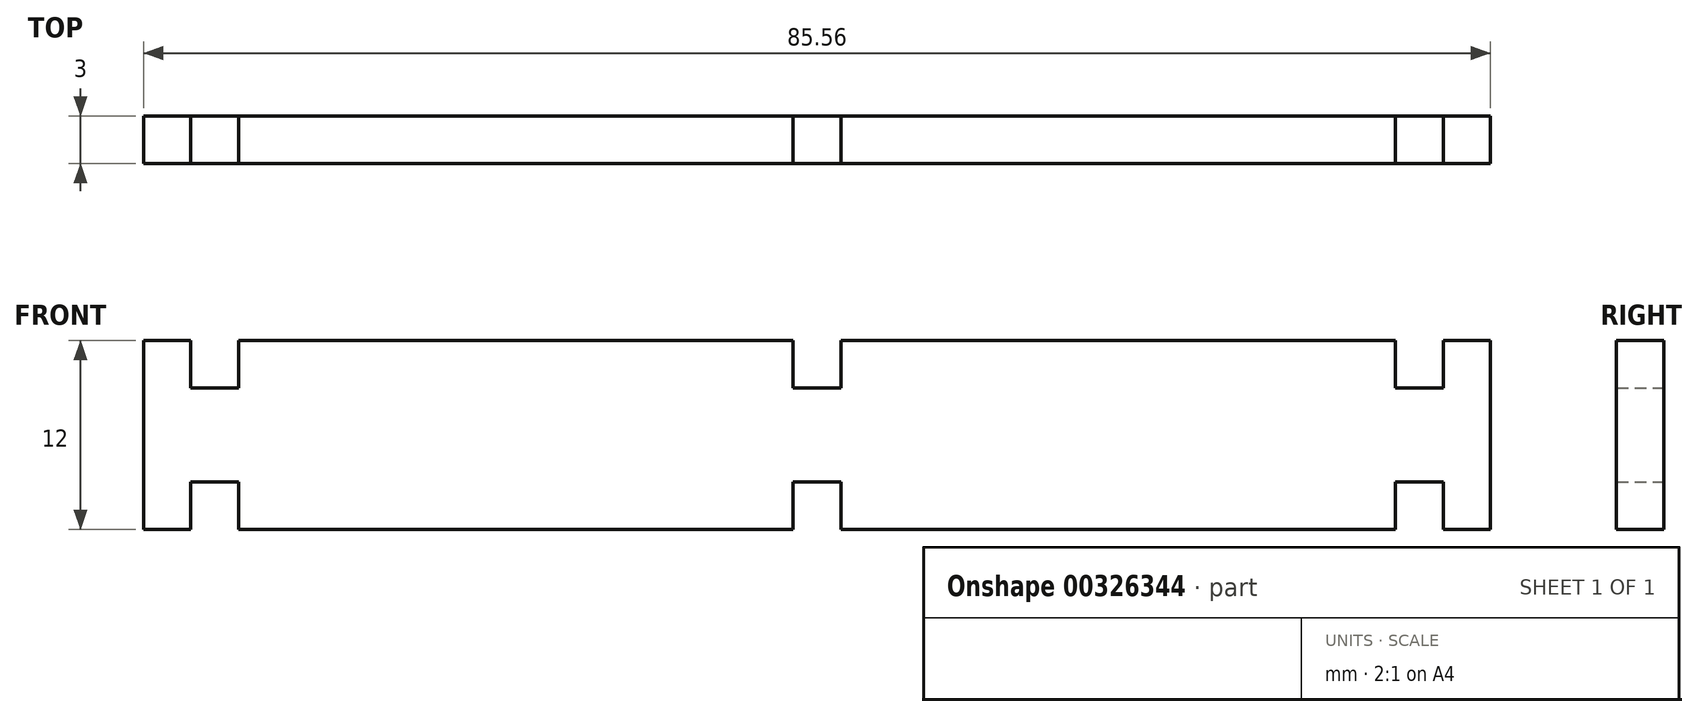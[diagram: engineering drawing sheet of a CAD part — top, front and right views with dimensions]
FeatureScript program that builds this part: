
annotation { "Feature Type Name" : "Feature", "Feature Type Description" : "" }
export const myFeature = defineFeature(function(context is Context, id is Id, definition is map)
    precondition{}
    {
        {
            var Q0;
            Q0=qCreatedBy(makeId("Front.planeOp"),FACE);
            var sketch = newSketch(context, id + "F0", { "sketchPlane" : qUnion([Q0])});
            skPoint(sketch, "E0", {"position": v(-39.78, 0) * mm});
            skPoint(sketch, "E1", {"position": v(-39.78, 3.02) * mm});
            skPoint(sketch, "E2", {"position": v(-36.74, 3.02) * mm});
            skPoint(sketch, "E3", {"position": v(39.78, 0) * mm});
            skPoint(sketch, "E4", {"position": v(39.78, 3.02) * mm});
            skPoint(sketch, "E5", {"position": v(36.74, 3.02) * mm});
            skPoint(sketch, "E6", {"position": v(36.74, 0) * mm});
            skLineSegment(sketch, "E7", {"start": v(-39.78, 0) * mm, "end": v(-39.78, 3.02) * mm});
            skLineSegment(sketch, "E8", {"start": v(-36.74, 3.02) * mm, "end": v(-39.78, 3.02) * mm});
            skLineSegment(sketch, "E9", {"start": v(-36.74, 0) * mm, "end": v(-36.74, 3.02) * mm});
            skLineSegment(sketch, "E10", {"start": v(36.74, 0) * mm, "end": v(36.74, 3.02) * mm});
            skLineSegment(sketch, "E11", {"start": v(39.78, 3.02) * mm, "end": v(36.74, 3.02) * mm});
            skLineSegment(sketch, "E12", {"start": v(39.78, 0) * mm, "end": v(39.78, 3.02) * mm});
            skLineSegment(sketch, "E13.trimOffspring", {"start": v(39.78, 0) * mm, "end": v(42.78, 0) * mm});
            skLineSegment(sketch, "E14.trimOffspring", {"start": v(-39.78, 0) * mm, "end": v(-42.78, 0) * mm});
            skLineSegment(sketch, "E15", {"start": v(-42.78, 12) * mm, "end": v(-39.78, 12) * mm});
            skLineSegment(sketch, "E16", {"start": v(-39.78, 12) * mm, "end": v(-39.78, 8.98) * mm});
            skLineSegment(sketch, "E17", {"start": v(-39.78, 8.98) * mm, "end": v(-36.74, 8.98) * mm});
            skLineSegment(sketch, "E18", {"start": v(-36.74, 8.98) * mm, "end": v(-36.74, 12) * mm});
            skLineSegment(sketch, "E19", {"start": v(42.78, 12) * mm, "end": v(39.78, 12) * mm});
            skLineSegment(sketch, "E20", {"start": v(39.78, 12) * mm, "end": v(39.78, 8.98) * mm});
            skLineSegment(sketch, "E21", {"start": v(39.78, 8.98) * mm, "end": v(36.74, 8.98) * mm});
            skLineSegment(sketch, "E22", {"start": v(36.74, 8.98) * mm, "end": v(36.74, 12) * mm});
            skLineSegment(sketch, "E23", {"start": v(36.74, 12) * mm, "end": v(1.52, 12) * mm});
            skLineSegment(sketch, "E24", {"start": v(42.78, 12) * mm, "end": v(42.78, 0) * mm});
            skLineSegment(sketch, "E25", {"start": v(-42.78, 12) * mm, "end": v(-42.78, 0) * mm});
            skLineSegment(sketch, "E26", {"start": v(-36.74, 0) * mm, "end": v(-1.52, 0) * mm});
            skLineSegment(sketch, "E27", {"start": v(-1.52, 12) * mm, "end": v(-1.52, 8.98) * mm});
            skLineSegment(sketch, "E28", {"start": v(1.52, 12) * mm, "end": v(1.52, 8.98) * mm});
            skLineSegment(sketch, "E29", {"start": v(-1.52, 0) * mm, "end": v(-1.52, 3.02) * mm});
            skLineSegment(sketch, "E30", {"start": v(1.52, 0) * mm, "end": v(1.52, 3.02) * mm});
            skLineSegment(sketch, "E31", {"start": v(-1.52, 3.02) * mm, "end": v(1.52, 3.02) * mm});
            skLineSegment(sketch, "E32", {"start": v(-1.52, 8.98) * mm, "end": v(1.52, 8.98) * mm});
            skLineSegment(sketch, "E33.trimOffspring", {"start": v(-1.52, 12) * mm, "end": v(-36.74, 12) * mm});
            skLineSegment(sketch, "E34.trimOffspring", {"start": v(1.52, 0) * mm, "end": v(36.74, 0) * mm});
            skSolve(sketch);
        }
        {
            var Q0;
            Q0=makeQuery(id+"F0.imprint","IMPRINT",FACE,{"disambiguationData":[TD([[makeQuery(id+"F0.imprint","IMPRINT",EDGE,{"derivedFrom":sQuery(id+"F0.wireOp",EDGE,"E7")}),1.0]])]});
            extrude(context, id + "F1", {"entities" : qUnion([Q0]), "depth" : 3 * mm});
        }
    });
